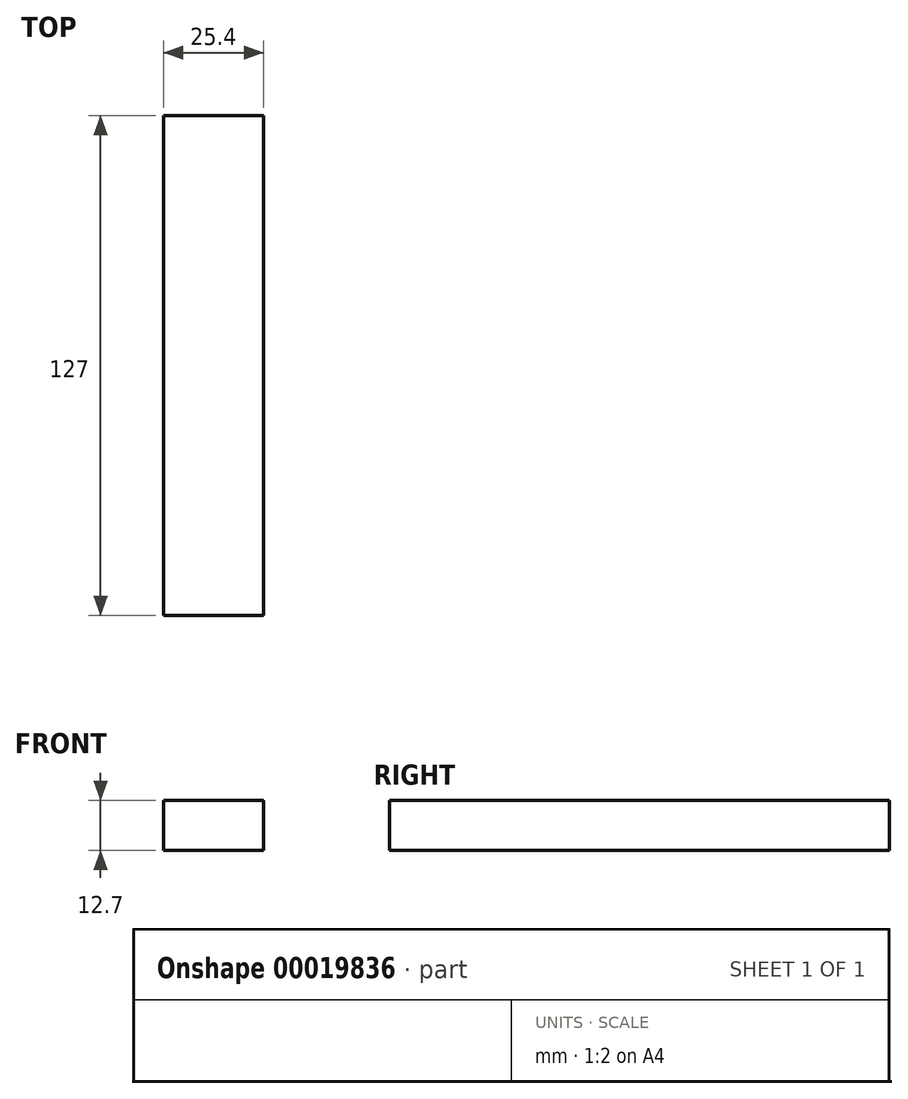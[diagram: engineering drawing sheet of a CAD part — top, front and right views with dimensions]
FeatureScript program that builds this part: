
annotation { "Feature Type Name" : "Feature", "Feature Type Description" : "" }
export const myFeature = defineFeature(function(context is Context, id is Id, definition is map)
    precondition{}
    {
        {
            var Q0;
            Q0=qCreatedBy(makeId("Front.planeOp"),FACE);
            var sketch = newSketch(context, id + "F0", { "sketchPlane" : qUnion([Q0])});
            skLineSegment(sketch, "E0.bottom", {"start": v(0, 0) * mm, "end": v(25.4, 0) * mm});
            skLineSegment(sketch, "E0.top", {"start": v(0, 12.7) * mm, "end": v(25.4, 12.7) * mm});
            skLineSegment(sketch, "E0.left", {"start": v(0, 0) * mm, "end": v(0, 12.7) * mm});
            skLineSegment(sketch, "E0.right", {"start": v(25.4, 0) * mm, "end": v(25.4, 12.7) * mm});
            skSolve(sketch);
        }
        {
            var Q0;
            Q0=makeQuery(id+"F0.imprint","IMPRINT",FACE,{"disambiguationData":[TD([[makeQuery(id+"F0.imprint","IMPRINT",EDGE,{"derivedFrom":sQuery(id+"F0.wireOp",EDGE,"E0.bottom")}),1.0]])]});
            extrude(context, id + "F1", {"entities" : qUnion([Q0]), "depth" : 127 * mm});
        }
    });
